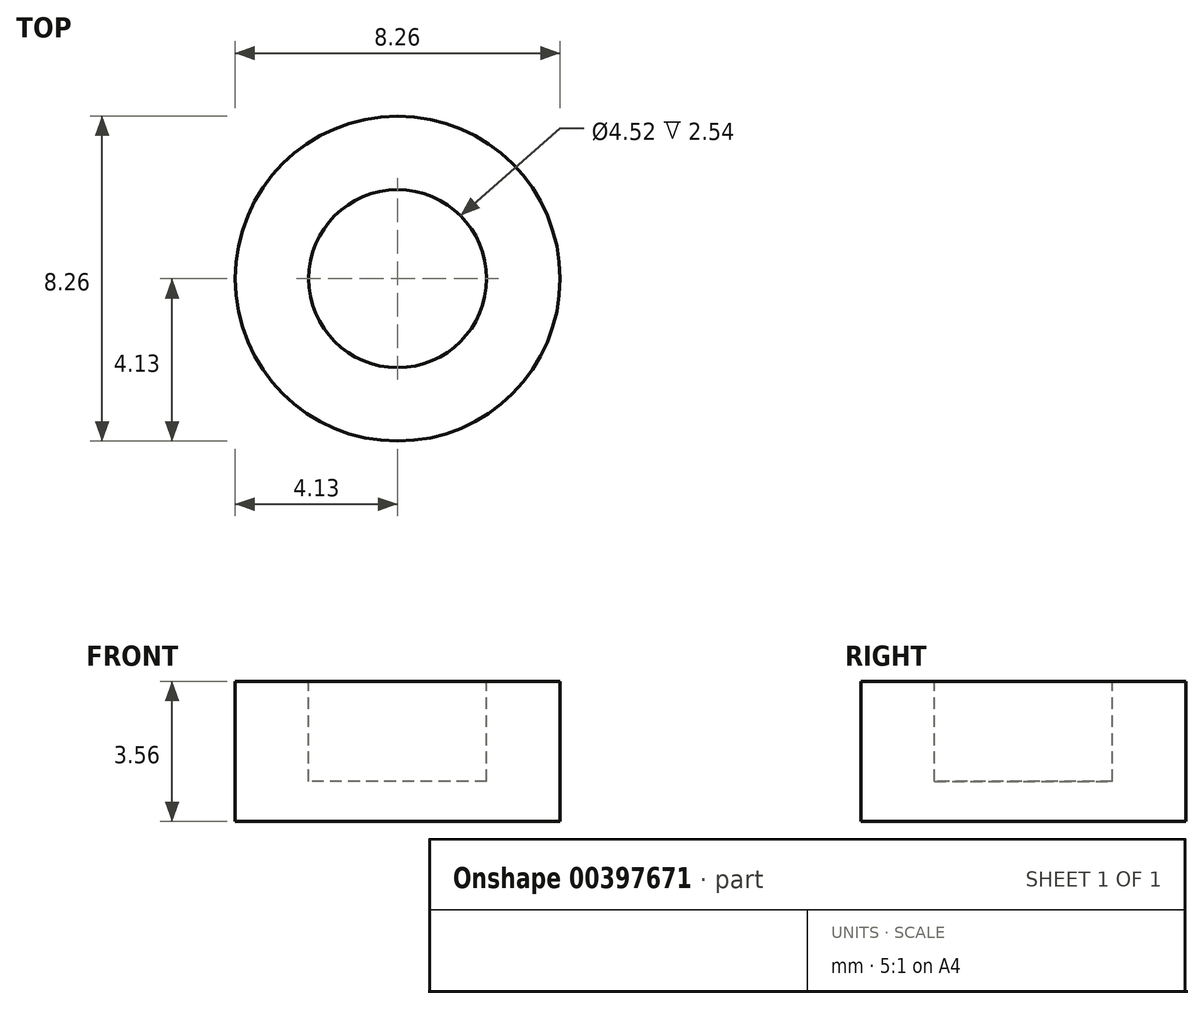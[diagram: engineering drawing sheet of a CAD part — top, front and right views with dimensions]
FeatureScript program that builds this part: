
annotation { "Feature Type Name" : "Feature", "Feature Type Description" : "" }
export const myFeature = defineFeature(function(context is Context, id is Id, definition is map)
    precondition{}
    {
        {
            var Q0;
            Q0=qCreatedBy(makeId("Top.planeOp"),FACE);
            var sketch = newSketch(context, id + "F0", { "sketchPlane" : qUnion([Q0])});
            skCircle(sketch, "E0", {"center": v(0, 0) * mm, "radius": 4.13 * mm});
            skSolve(sketch);
        }
        {
            var Q0;
            Q0 = qSketchRegion(id + "F0", true);
            extrude(context, id + "F1", {"entities" : qUnion([Q0]), "depth" : 3.56 * mm, "offsetDistance" : 25.4 * mm});
        }
        {
            var Q0;
            Q0=makeQuery(id+"F1.opExtrude","CAP_FACE",FACE,{"disambiguationData":[OSD([sQuery(id+"F0.wireOp",EDGE,"E0")])],"isStart":false});
            var sketch = newSketch(context, id + "F2", { "sketchPlane" : qUnion([Q0])});
            skCircle(sketch, "E1", {"center": v(0, 0) * mm, "radius": 2.26 * mm});
            skSolve(sketch);
        }
        {
            var Q0;
            Q0 = qSketchRegion(id + "F2", true);
            extrude(context, id + "F3", {"entities" : qUnion([Q0]), "operationType" : NewBodyOperationType.REMOVE, "oppositeDirection" : true, "depth" : 2.54 * mm, "offsetDistance" : 25.4 * mm});
        }
    });
